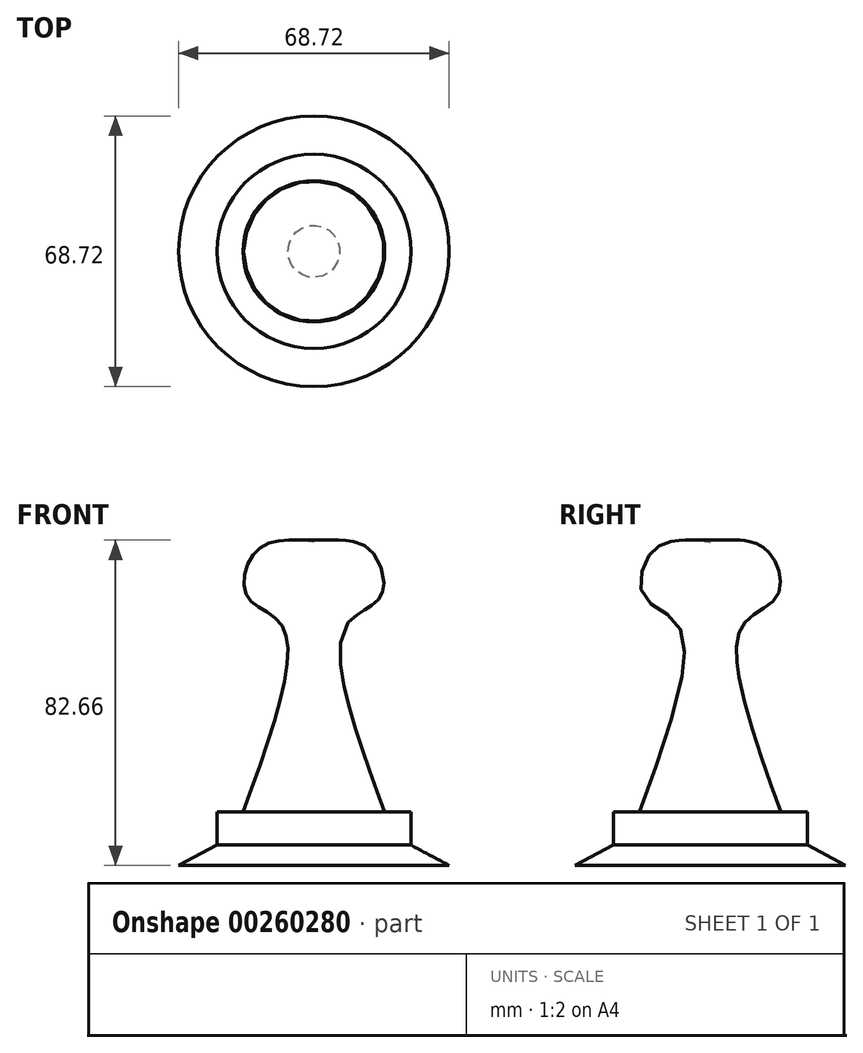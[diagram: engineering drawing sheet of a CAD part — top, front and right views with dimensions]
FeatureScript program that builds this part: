
annotation { "Feature Type Name" : "Feature", "Feature Type Description" : "" }
export const myFeature = defineFeature(function(context is Context, id is Id, definition is map)
    precondition{}
    {
        {
            var Q0;
            Q0=qCreatedBy(makeId("Front.planeOp"),FACE);
            var sketch = newSketch(context, id + "F0", { "sketchPlane" : qUnion([Q0])});
            skFitSpline(sketch, "E0", {"points": [v(0, 68.65) * mm, v(-14.04, 66.83) * mm, v(-17.07, 55) * mm, v(-7.97, 47.12) * mm, v(-17.98, 0) * mm], "startDerivative": vector(-74.57, 8.02) * mm, "endDerivative": vector(-55.1, -150.72) * mm});
            skLineSegment(sketch, "E1", {"start": v(-17.98, 0) * mm, "end": v(-24.65, 0) * mm});
            skLineSegment(sketch, "E2", {"start": v(-24.65, 0) * mm, "end": v(-24.65, -8.39) * mm});
            skLineSegment(sketch, "E3", {"start": v(-24.65, -8.39) * mm, "end": v(-34.36, -13.55) * mm});
            skLineSegment(sketch, "E4", {"start": v(-34.36, -13.55) * mm, "end": v(0, -13.55) * mm});
            skLineSegment(sketch, "E5", {"start": v(0, 68.65) * mm, "end": v(0, -13.55) * mm});
            skLineSegment(sketch, "E6", {"start": v(0, 104.75) * mm, "end": v(0, -41.45) * mm, "construction": true});
            skSolve(sketch);
        }
        {
            var Q0;
            Q0=makeQuery(id+"F0.imprint","IMPRINT",FACE,{"disambiguationData":[TD([[makeQuery(id+"F0.imprint","IMPRINT",EDGE,{"derivedFrom":sQuery(id+"F0.wireOp",EDGE,"E0")}),1.0]])]});
            var Q1;
            Q1=sQuery(id+"F0.wireOp",EDGE,"E6");
            revolve(context, id + "F1", {"entities" : qUnion([Q0]), "axis" : qUnion([Q1]), "revolveType" : RevolveType.FULL});
        }
    });
